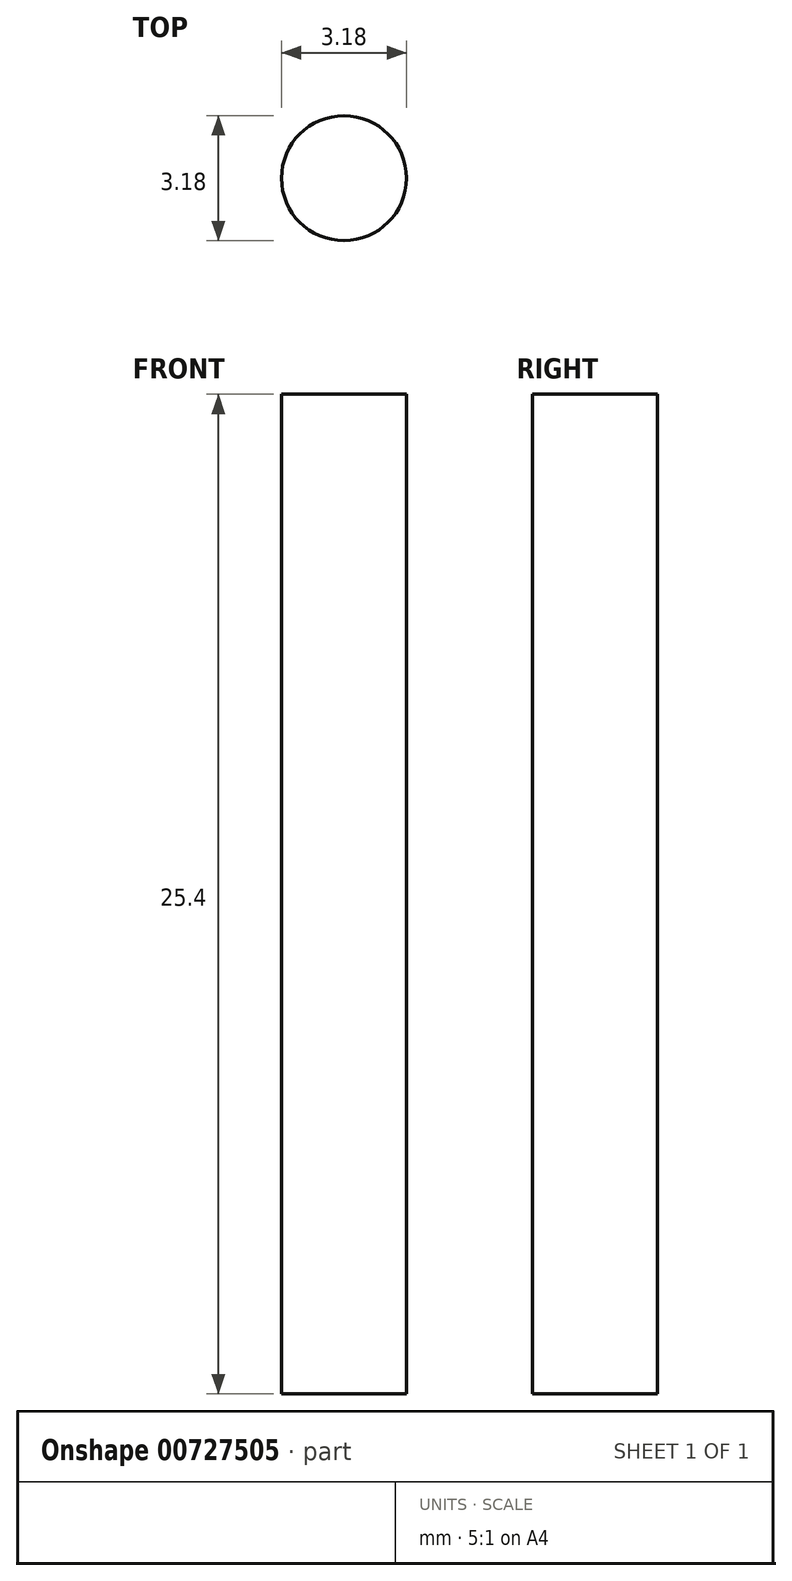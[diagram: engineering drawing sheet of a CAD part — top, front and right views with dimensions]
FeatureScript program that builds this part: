
annotation { "Feature Type Name" : "Feature", "Feature Type Description" : "" }
export const myFeature = defineFeature(function(context is Context, id is Id, definition is map)
    precondition{}
    {
        {
            var Q0;
            Q0=qCreatedBy(makeId("Top.planeOp"),FACE);
            var sketch = newSketch(context, id + "F0", { "sketchPlane" : qUnion([Q0])});
            skCircle(sketch, "E0", {"center": v(-22.53, 18.88) * mm, "radius": 1.59 * mm});
            skCircle(sketch, "E1", {"center": v(12.84, 18.32) * mm, "radius": 1.59 * mm});
            skSolve(sketch);
        }
        {
            var Q0;
            Q0=makeQuery(id+"F0.imprint","IMPRINT",FACE,{"disambiguationData":[TD([[makeQuery(id+"F0.imprint","IMPRINT",EDGE,{"derivedFrom":sQuery(id+"F0.wireOp",EDGE,"E0")}),1.0]])]});
            extrude(context, id + "F1", {"entities" : qUnion([Q0]), "depth" : 25.4 * mm, "offsetDistance" : 25.4 * mm});
        }
    });
